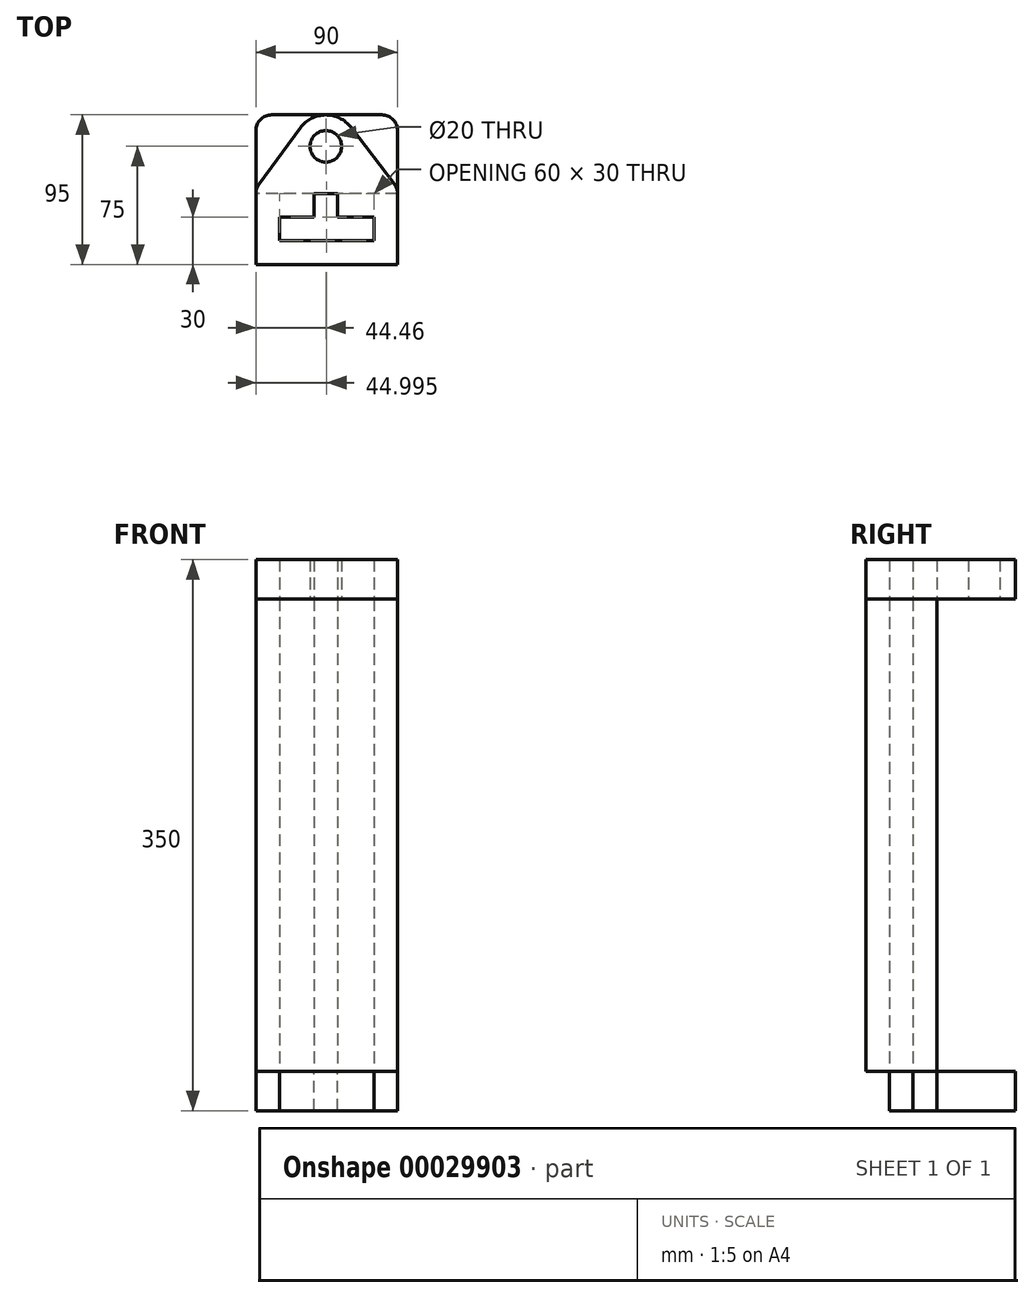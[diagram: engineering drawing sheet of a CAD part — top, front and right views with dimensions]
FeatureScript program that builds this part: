
annotation { "Feature Type Name" : "Feature", "Feature Type Description" : "" }
export const myFeature = defineFeature(function(context is Context, id is Id, definition is map)
    precondition{}
    {
        {
            var Q0;
            Q0=qCreatedBy(makeId("Top.planeOp"),FACE);
            var sketch = newSketch(context, id + "F0", { "sketchPlane" : qUnion([Q0])});
            skLineSegment(sketch, "E0", {"start": v(0, 0) * mm, "end": v(30.54, 0) * mm});
            skLineSegment(sketch, "E1", {"start": v(30.54, 0) * mm, "end": v(-29.46, 0) * mm});
            skLineSegment(sketch, "E2", {"start": v(-29.46, 0) * mm, "end": v(-29.46, 15) * mm});
            skLineSegment(sketch, "E3", {"start": v(-29.46, 15) * mm, "end": v(-7.5, 15) * mm});
            skLineSegment(sketch, "E4", {"start": v(30.54, 15) * mm, "end": v(30.54, 0) * mm});
            skLineSegment(sketch, "E5.trimOffspring", {"start": v(7.5, 15) * mm, "end": v(30.54, 15) * mm});
            skLineSegment(sketch, "E6", {"start": v(-7.5, 15) * mm, "end": v(-7.5, 30) * mm});
            skLineSegment(sketch, "E7", {"start": v(-7.5, 30) * mm, "end": v(-44.46, 30) * mm});
            skLineSegment(sketch, "E8", {"start": v(-44.46, 30) * mm, "end": v(-44.46, -15) * mm});
            skLineSegment(sketch, "E9", {"start": v(-44.46, -15) * mm, "end": v(45.54, -15) * mm});
            skLineSegment(sketch, "E10", {"start": v(45.54, -15) * mm, "end": v(45.54, 30) * mm});
            skLineSegment(sketch, "E11", {"start": v(45.54, 30) * mm, "end": v(7.5, 30) * mm});
            skLineSegment(sketch, "E12", {"start": v(7.5, 30) * mm, "end": v(7.5, 15) * mm});
            skPoint(sketch, "E13.MirrorCS.start.orphan", {"position": v(-7.5, 0) * mm});
            skPoint(sketch, "E14.start.orphan", {"position": v(7.5, 0) * mm});
            skSolve(sketch);
        }
        {
            var Q0;
            Q0 = qSketchRegion(id + "F0", true);
            extrude(context, id + "F1", {"entities" : qUnion([Q0]), "depth" : 300 * mm});
        }
        {
            var Q0;
            Q0=makeQuery(id+"F1.opExtrude","CAP_FACE",FACE,{"disambiguationData":[OSD([sQuery(id+"F0.wireOp",EDGE,"E1"),sQuery(id+"F0.wireOp",EDGE,"E2"),sQuery(id+"F0.wireOp",EDGE,"E3"),sQuery(id+"F0.wireOp",EDGE,"E4"),sQuery(id+"F0.wireOp",EDGE,"E5.trimOffspring"),sQuery(id+"F0.wireOp",EDGE,"E6"),sQuery(id+"F0.wireOp",EDGE,"E7"),sQuery(id+"F0.wireOp",EDGE,"E8"),sQuery(id+"F0.wireOp",EDGE,"E9"),sQuery(id+"F0.wireOp",EDGE,"E10"),sQuery(id+"F0.wireOp",EDGE,"E11"),sQuery(id+"F0.wireOp",EDGE,"E12")])],"isStart":false});
            var sketch = newSketch(context, id + "F2", { "sketchPlane" : qUnion([Q0])});
            skLineSegment(sketch, "E15", {"start": v(-44.46, 30) * mm, "end": v(45.54, 30) * mm});
            skCircle(sketch, "E16", {"center": v(0, 60) * mm, "radius": 10 * mm});
            skArc(sketch, "E17", {"start": v(15.89, 72.15) * mm, "mid": v(-0.2, 80) * mm, "end": v(-16.11, 71.85) * mm});
            skArc(sketch, "E18", {"start": v(-42.52, 35.92) * mm, "mid": v(-43.97, 33.12) * mm, "end": v(-44.46, 30) * mm});
            skLineSegment(sketch, "E19", {"start": v(-42.52, 35.92) * mm, "end": v(-16.11, 71.85) * mm});
            skLineSegment(sketch, "E20", {"start": v(45.54, 30) * mm, "end": v(35.54, 30) * mm});
            skArc(sketch, "E21", {"start": v(45.54, 30) * mm, "mid": v(45, 33.2) * mm, "end": v(43.48, 36.08) * mm});
            skLineSegment(sketch, "E22", {"start": v(15.89, 72.15) * mm, "end": v(43.48, 36.08) * mm});
            skPoint(sketch, "E23.orphan", {"position": v(0, 30) * mm});
            skSolve(sketch);
        }
        {
            var Q0;
            Q0=makeQuery(id+"F2.imprint","IMPRINT",FACE,{"disambiguationData":[TD([[makeQuery(id+"F2.imprint","IMPRINT",EDGE,{"derivedFrom":sQuery(id+"F2.wireOp",EDGE,"E16")}),-1.0]])]});
            var Q1;
            {var subQ3=sQuery(id+"F2.wireOp",EDGE,"E20");Q1=makeQuery(id+"F2.imprint","IMPRINT",FACE,{"disambiguationData":[TD([[makeQuery(id+"F2.imprint","IMPRINT",EDGE,{"derivedFrom":subQ3}),1.0]])]});}
            var Q2;
            Q2=makeQuery(id+"F2.imprint","IMPRINT",FACE,{"disambiguationData":[TD([[makeQuery(id+"F2.imprint","IMPRINT",EDGE,{"derivedFrom":makeQuery(id+"F1.opExtrude","CAP_EDGE",EDGE,{"disambiguationData":[OSD([sQuery(id+"F0.wireOp",EDGE,"E1")])],"isStart":false})}),-1.0]])]});
            extrude(context, id + "F3", {"entities" : qUnion([Q0, Q1, Q2]), "depth" : 25 * mm});
        }
        {
            var Q0;
            Q0=makeQuery(id+"F1.opExtrude","CAP_FACE",FACE,{"disambiguationData":[OSD([sQuery(id+"F0.wireOp",EDGE,"E1"),sQuery(id+"F0.wireOp",EDGE,"E2"),sQuery(id+"F0.wireOp",EDGE,"E3"),sQuery(id+"F0.wireOp",EDGE,"E4"),sQuery(id+"F0.wireOp",EDGE,"E5.trimOffspring"),sQuery(id+"F0.wireOp",EDGE,"E6"),sQuery(id+"F0.wireOp",EDGE,"E7"),sQuery(id+"F0.wireOp",EDGE,"E8"),sQuery(id+"F0.wireOp",EDGE,"E9"),sQuery(id+"F0.wireOp",EDGE,"E10"),sQuery(id+"F0.wireOp",EDGE,"E11"),sQuery(id+"F0.wireOp",EDGE,"E12")])],"isStart":true});
            var sketch = newSketch(context, id + "F4", { "sketchPlane" : qUnion([Q0])});
            skLineSegment(sketch, "E24", {"start": v(45.54, -30) * mm, "end": v(45.54, -70) * mm});
            skLineSegment(sketch, "E25", {"start": v(-44.46, -30) * mm, "end": v(-44.46, -70) * mm});
            skLineSegment(sketch, "E26", {"start": v(-34.46, -80) * mm, "end": v(35.54, -80) * mm});
            skArc(sketch, "E27", {"start": v(35.54, -80) * mm, "mid": v(42.6, -77.07) * mm, "end": v(45.54, -70) * mm});
            skArc(sketch, "E28", {"start": v(-44.46, -70) * mm, "mid": v(-41.54, -77.07) * mm, "end": v(-34.46, -80) * mm});
            skPoint(sketch, "E29.orphan", {"position": v(45.54, -80) * mm});
            skPoint(sketch, "E30.orphan", {"position": v(-44.46, -80) * mm});
            skSolve(sketch);
        }
        {
            var Q0;
            Q0 = qSketchRegion(id + "F4", true);
            var Q1;
            Q1=makeQuery(id+"F4.imprint","IMPRINT",FACE,{"disambiguationData":[TD([[makeQuery(id+"F4.imprint","IMPRINT",EDGE,{"derivedFrom":sQuery(id+"F4.wireOp",EDGE,"E24")}),-1.0]])]});
            var Q2;
            Q2=makeQuery(id+"F4.imprint","IMPRINT",FACE,{"disambiguationData":[TD([[makeQuery(id+"F4.imprint","IMPRINT",EDGE,{"derivedFrom":makeQuery(id+"F1.opExtrude","CAP_EDGE",EDGE,{"disambiguationData":[OSD([sQuery(id+"F0.wireOp",EDGE,"E1")])],"isStart":true})}),-1.0]])]});
            extrude(context, id + "F5", {"entities" : qUnion([Q0, Q1, Q2]), "operationType" : NewBodyOperationType.ADD, "depth" : 25 * mm});
        }
    });
